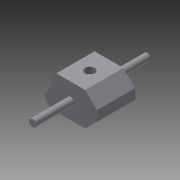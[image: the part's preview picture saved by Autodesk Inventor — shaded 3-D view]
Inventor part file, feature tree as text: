
AUTODESK INVENTOR PART (.ipt)
format: ipt  version: 2014 (Build 180170000, 170)  size: 141,824 bytes
history: native  units: in
note: dims shown in document units (in); Inventor stores cm internally (conversion verified against a paired STEP export)
features: extrude x8, sketch x8
ambient origin geometry x8: Origin, YZ Plane, XZ Plane, XY Plane, X Axis, Y Axis, Z Axis, Center Point
bodies: Solid1 (feature_tree)
feature tree (16):
  extrude  "Extrusion1"  Depth=8.0in TaperAngle=0.0deg
  extrude  "Extrusion2"  Depth=1.5in TaperAngle=0.0deg
  sketch  "Sketch4"  dims[d22=1.5in d23=1.5in]
  extrude  "Extrusion4"  Depth=1.5in
  extrude  "Extrusion5"  Depth=8.0in TaperAngle=0.0deg
  extrude  "Extrusion6"  Depth=0.75in TaperAngle=0.0deg
  extrude  "Extrusion7"  Depth=2.0in TaperAngle=0.0deg
  extrude  "Extrusion8"  Depth=2.0in
  extrude  "Extrusion10"  [1 undecoded]
  sketch  "Sketch1"  dims[d9=2.0in d14=8.0in d15=0.0in]
  sketch  "Sketch2"  dims[d16=2.0in d17=1.5in d18=0.0in]
  sketch  "Sketch5"  dims[d24=8.0in d25=0.0in d26=8.0in d27=0.0in]
  sketch  "Sketch6"  dims[d30=1.5in d31=0.0in d32=0.75in d33=0.0in]
  sketch  "Sketch7"  dims[d34=1.0in d35=2.0in d36=0.0in]
  sketch  "Sketch8"  dims[d37=2.0in d38=0.0in d42=2.5in]
  sketch  "Sketch10"  dims[d43=0.2in d44=0.0in]
note: 1 required parameter value undecoded (feature->parameter linkage not recoverable at this tier; creation-order binding heuristic only, values carry confidence <= 0.55)
